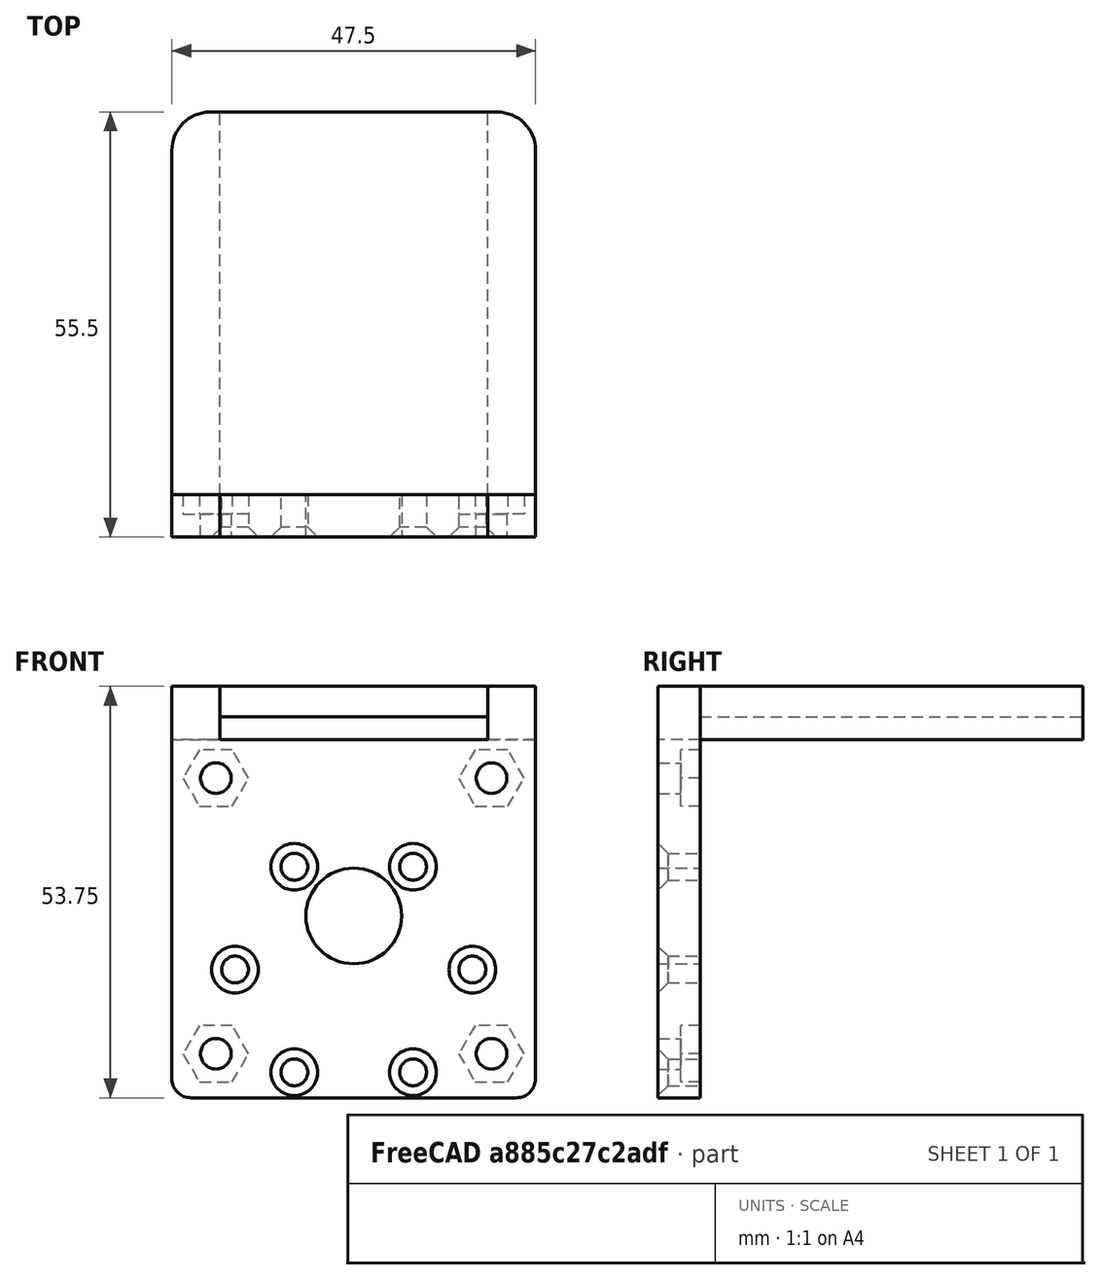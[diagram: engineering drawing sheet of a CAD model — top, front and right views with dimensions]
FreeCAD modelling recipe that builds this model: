
FCSTD DOCUMENT  (FreeCAD 1.0R39109 (Git))
Label: PUMP
License: All rights reserved
LicenseURL: http://en.wikipedia.org/wiki/All_rights_reserved
objects: Sketcher::SketchObject×4, PartDesign::Pad×2, PartDesign::Pocket×2, PartDesign::Body×2, PartDesign::Chamfer×1, Mesh::Feature×1
note: 25 computed .brp shape members not serialized (recipe doc carries the construction recipe); baked Part::Feature solids carry a one-line shape summary decoded from their .brp

FEATURE [Sketcher::SketchObject] Sketch
  ArcFitTolerance = 0
  AttachmentSupport = -> [XZ_Plane001]
  FullyConstrained = false
  MakeInternals = false
  MapMode = 5
  Placement = pos=(0,0,0) rot=(1,0,0;1.5708rad)
  sketch-geometry (46):
    g0: GeomPoint [constr] X=0 Y=0 Z=0
    g1: Circle [constr] CenterX=0 CenterY=0 CenterZ=0 NormalX=0 NormalY=0 NormalZ=1 AngleXU=0 Radius=15.5
    g2: LineSegment [constr] StartX=0 StartY=0 StartZ=0 EndX=-7.75 EndY=13.4234 EndZ=0
    g3: LineSegment [constr] StartX=0 StartY=0 StartZ=0 EndX=0 EndY=15.5 EndZ=0
    g4: Circle CenterX=0 CenterY=7 CenterZ=0 NormalX=0 NormalY=0 NormalZ=1 AngleXU=0 Radius=6.25
    g5: Circle CenterX=-7.75 CenterY=13.4234 CenterZ=0 NormalX=0 NormalY=0 NormalZ=1 AngleXU=0 Radius=1.75
    g6: LineSegment [constr] StartX=-7.75 StartY=13.4234 StartZ=0 EndX=-15.5 EndY=3.6e-15 EndZ=0
    g7: LineSegment [constr] StartX=-15.5 StartY=3.6e-15 StartZ=0 EndX=-7.75 EndY=-13.4234 EndZ=0
    g8: LineSegment [constr] StartX=-7.75 StartY=-13.4234 StartZ=0 EndX=7.75 EndY=-13.4234 EndZ=0
    g9: LineSegment [constr] StartX=7.75 StartY=-13.4234 StartZ=0 EndX=15.5 EndY=-3.6e-15 EndZ=0
    g10: LineSegment [constr] StartX=15.5 StartY=-3.6e-15 StartZ=0 EndX=7.75 EndY=13.4234 EndZ=0
    g11: LineSegment [constr] StartX=7.75 StartY=13.4234 StartZ=0 EndX=-7.75 EndY=13.4234 EndZ=0
    g12: Circle [constr] CenterX=0 CenterY=0 CenterZ=0 NormalX=0 NormalY=0 NormalZ=1 AngleXU=0 Radius=15.5
    g13: Circle CenterX=-15.5 CenterY=3.6e-15 CenterZ=0 NormalX=0 NormalY=0 NormalZ=1 AngleXU=0 Radius=1.75
    g14: Circle CenterX=-7.75 CenterY=-13.4234 CenterZ=0 NormalX=0 NormalY=0 NormalZ=1 AngleXU=0 Radius=1.75
    g15: Circle CenterX=7.75 CenterY=-13.4234 CenterZ=0 NormalX=0 NormalY=0 NormalZ=1 AngleXU=0 Radius=1.75
    g16: Circle CenterX=15.5 CenterY=-3.6e-15 CenterZ=0 NormalX=0 NormalY=0 NormalZ=1 AngleXU=0 Radius=1.75
    g17: Circle CenterX=7.75 CenterY=13.4234 CenterZ=0 NormalX=0 NormalY=0 NormalZ=1 AngleXU=0 Radius=1.75
    g18: LineSegment [constr] StartX=-13.4234 StartY=7.75 StartZ=0 EndX=0 EndY=-15.5 EndZ=0
    g19: LineSegment [constr] StartX=0 StartY=-15.5 StartZ=0 EndX=13.4234 EndY=7.75 EndZ=0
    g20: LineSegment [constr] StartX=13.4234 StartY=7.75 StartZ=0 EndX=-13.4234 EndY=7.75 EndZ=0
    g21: Circle [constr] CenterX=0 CenterY=0 CenterZ=0 NormalX=0 NormalY=0 NormalZ=1 AngleXU=0 Radius=15.5
    g22: Circle [constr] CenterX=0 CenterY=0 CenterZ=0 NormalX=0 NormalY=0 NormalZ=1 AngleXU=0 Radius=18.5
    g23: GeomPoint [constr] X=0 Y=0 Z=0
    g24: LineSegment [constr] StartX=-18 StartY=-11 StartZ=0 EndX=-18 EndY=25 EndZ=0
    g25: LineSegment [constr] StartX=-18 StartY=25 StartZ=0 EndX=18 EndY=25 EndZ=0
    g26: LineSegment [constr] StartX=18 StartY=25 StartZ=0 EndX=18 EndY=-11 EndZ=0
    g27: LineSegment [constr] StartX=18 StartY=-11 StartZ=0 EndX=-18 EndY=-11 EndZ=0
    g28: GeomPoint [constr] X=0 Y=7 Z=0
    g29: Circle CenterX=-18 CenterY=25 CenterZ=0 NormalX=0 NormalY=0 NormalZ=1 AngleXU=0 Radius=2
    g30: Circle CenterX=18 CenterY=25 CenterZ=0 NormalX=0 NormalY=0 NormalZ=1 AngleXU=0 Radius=2
    g31: Circle CenterX=18 CenterY=-11 CenterZ=0 NormalX=0 NormalY=0 NormalZ=1 AngleXU=0 Radius=2
    g32: Circle CenterX=-18 CenterY=-11 CenterZ=0 NormalX=0 NormalY=0 NormalZ=1 AngleXU=0 Radius=2
    g33: LineSegment StartX=21.25 StartY=-16.75 StartZ=0 EndX=-21.25 EndY=-16.75 EndZ=0
    g34: GeomPoint [constr] X=0 Y=7 Z=0
    g35: ArcOfCircle CenterX=-21.25 CenterY=-14.25 CenterZ=0 NormalX=0 NormalY=0 NormalZ=1 AngleXU=0 Radius=2.5 StartAngle=3.14159 EndAngle=4.71239
    g36: GeomPoint [constr] X=-23.75 Y=-16.75 Z=0
    g37: ArcOfCircle CenterX=21.25 CenterY=-14.25 CenterZ=0 NormalX=0 NormalY=0 NormalZ=1 AngleXU=0 Radius=2.5 StartAngle=4.71239 EndAngle=6.28319
    g38: GeomPoint [constr] X=23.75 Y=-16.75 Z=0
    g39: LineSegment StartX=-23.75 StartY=37 StartZ=0 EndX=-17.5 EndY=37 EndZ=0
    g40: LineSegment StartX=-17.5 StartY=37 StartZ=0 EndX=-17.5 EndY=30 EndZ=0
    g41: LineSegment StartX=-17.5 StartY=30 StartZ=0 EndX=17.5 EndY=30 EndZ=0
    g42: LineSegment StartX=17.5 StartY=30 StartZ=0 EndX=17.5 EndY=37 EndZ=0
    g43: LineSegment StartX=17.5 StartY=37 StartZ=0 EndX=23.75 EndY=37 EndZ=0
    g44: LineSegment StartX=23.75 StartY=37 StartZ=0 EndX=23.75 EndY=-14.25 EndZ=0
    g45: LineSegment StartX=-23.75 StartY=37 StartZ=0 EndX=-23.75 EndY=-14.25 EndZ=0
  constraints (103):
    c: Coincident(g0,g-1)
    c: Coincident(g1,g0)
    c: Coincident(g2,g0)
    c: PointOnObject(g2,g1)
    c: Coincident(g3,g0)
    c: PointOnObject(g3,g1)
    c: Vertical(g3)
    c: Angle(g3,g2) = 0.523599
    c: PointOnObject(g4,g3)
    c: DistanceY(g0,g4) = 7
    c: Coincident(g5,g2)
    c: Diameter(g1) = 31
    c: Coincident(g6,g7)
    c: Coincident(g7,g8)
    c: Coincident(g8,g9)
    c: Coincident(g9,g10)
    c: Coincident(g10,g11)
    c: Coincident(g11,g6)
    c: Equal(g6, g7-g11) x5
    c: PointOnObject(g6,g12)
    c: PointOnObject(g7,g12)
    c: PointOnObject(g8,g12)
    c: PointOnObject(g9,g12)
    c: PointOnObject(g10,g12)
    c: PointOnObject(g11,g12)
    c: Coincident(g12,g0)
    c: Coincident(g11,g2)
    c: Coincident(g13,g6)
    c: Coincident(g14,g7)
    c: Coincident(g15,g8)
    c: Coincident(g16,g9)
    c: Coincident(g17,g10)
    c: Equal(g14,g13)
    c: Equal(g13,g5)
    c: Equal(g5,g17)
    c: Equal(g17,g15)
    c: Equal(g15,g16)
    c: Coincident(g18,g19)
    c: Coincident(g19,g20)
    c: Coincident(g20,g18)
    c: Equal(g18,g19)
    c: Equal(g18,g20)
    c: PointOnObject(g18,g21)
    c: PointOnObject(g19,g21)
    c: PointOnObject(g20,g21)
    c: Coincident(g21,g0)
    c: PointOnObject(g20,g1)
    c: Horizontal(g20)
    c: Coincident(g22,g0)
    c: Diameter(g22) = 37
    c: Diameter(g17) = 3.5
    c: Diameter(g4) = 12.5
    c: Coincident(g23,g0)
    c: Coincident(g24,g25)
    c: Coincident(g25,g26)
    c: Coincident(g26,g27)
    c: Coincident(g27,g24)
    c: Horizontal(g25)
    c: Horizontal(g27)
    c: Vertical(g24)
    c: Vertical(g26)
    c: Symmetric(g25,g24,g28)
    c: Coincident(g28,g4)
    c: DistanceX(g25,g25) = 36
    c: Equal(g25,g24)
    c: Coincident(g29,g24)
    c: Coincident(g30,g25)
    c: Coincident(g31,g26)
    c: Coincident(g32,g24)
    c: Equal(g32,g31)
    c: Equal(g31,g29)
    c: Equal(g29,g30)
    c: Diameter(g29) = 4
    c: Horizontal(g33)
    c: Coincident(g34,g4)
    c: DistanceY(g36,g-1) = 16.75
    c: PointOnObject(g36,g33)
    c: Tangent(g33,g35) = 1.5708
    c: PointOnObject(g38,g33)
    c: Tangent(g33,g37) = 1.5708
    c: Diameter(g35) = 5
    c: Horizontal(g39)
    c: Coincident(g39,g40)
    c: Vertical(g40)
    c: Coincident(g40,g41)
    c: Horizontal(g41)
    c: Coincident(g41,g42)
    c: Vertical(g42)
    c: Coincident(g42,g43)
    c: Horizontal(g43)
    c: Equal(g39,g43)
    c: DistanceX(g39,g42) = 35
    c: DistanceX(g39,g43) = 47.5  'width'
    c: Coincident(g44,g43)
    c: Tangent(g44,g37) = 1.5708
    c: Vertical(g44)
    c: Symmetric(g35,g37,g-2)
    c: Horizontal(g42,g39)
    c: Coincident(g45,g39)
    c: Tangent(g45,g35) = -1.5708
    c: Vertical(g45)
    c: DistanceY(g-1,g40) = 30  'Walloffset'
    c: DistanceY(g40,g39) = 7  'wall'
FEATURE [PartDesign::Pad] Pad
  Direction = (0,-1,2e-16)
  Length = 5.5
  Length2 = 10
  Placement = pos=(0,0,0) rot=(1,0,0;1.5708rad)
  Profile = -> Sketch
  ReferenceAxis = -> Sketch [N_Axis]
  Suppressed = false
  Type = 0
FEATURE [PartDesign::Chamfer] Chamfer
  Angle = 45
  Base = -> Pad [Edge63,Edge51,Edge48,Edge60,Edge54,Edge57]
  BaseFeature = -> Pad
  ChamferType = 0
  FlipDirection = false
  Placement = pos=(0,0,0) rot=(1,0,0;1.5708rad)
  Size = 1.3
  Size2 = 1
  SupportTransform = false
  Suppressed = false
  UseAllEdges = false
FEATURE [Sketcher::SketchObject] Sketch001
  ArcFitTolerance = 0
  AttachmentSupport = -> [XZ_Plane001]
  ExternalGeometry = -> [Chamfer]
  FullyConstrained = true
  MakeInternals = false
  MapMode = 5
  Placement = pos=(0,0,0) rot=(1,0,0;1.5708rad)
  sketch-geometry (28):
    g0: LineSegment StartX=-15.8638 StartY=28.7 StartZ=0 EndX=-20.1362 EndY=28.7 EndZ=0
    g1: LineSegment StartX=-20.1362 StartY=28.7 StartZ=0 EndX=-22.2724 EndY=25 EndZ=0
    g2: LineSegment StartX=-22.2724 StartY=25 StartZ=0 EndX=-20.1362 EndY=21.3 EndZ=0
    g3: LineSegment StartX=-20.1362 StartY=21.3 StartZ=0 EndX=-15.8638 EndY=21.3 EndZ=0
    g4: LineSegment StartX=-15.8638 StartY=21.3 StartZ=0 EndX=-13.7276 EndY=25 EndZ=0
    g5: LineSegment StartX=-13.7276 StartY=25 StartZ=0 EndX=-15.8638 EndY=28.7 EndZ=0
    g6: Circle [constr] CenterX=-18 CenterY=25 CenterZ=0 NormalX=0 NormalY=0 NormalZ=1 AngleXU=0 Radius=4.27239
    g7: LineSegment StartX=20.1362 StartY=28.7 StartZ=0 EndX=15.8638 EndY=28.7 EndZ=0
    g8: LineSegment StartX=15.8638 StartY=28.7 StartZ=0 EndX=13.7276 EndY=25 EndZ=0
    g9: LineSegment StartX=13.7276 StartY=25 StartZ=0 EndX=15.8638 EndY=21.3 EndZ=0
    g10: LineSegment StartX=15.8638 StartY=21.3 StartZ=0 EndX=20.1362 EndY=21.3 EndZ=0
    g11: LineSegment StartX=20.1362 StartY=21.3 StartZ=0 EndX=22.2724 EndY=25 EndZ=0
    g12: LineSegment StartX=22.2724 StartY=25 StartZ=0 EndX=20.1362 EndY=28.7 EndZ=0
    g13: Circle [constr] CenterX=18 CenterY=25 CenterZ=0 NormalX=0 NormalY=0 NormalZ=1 AngleXU=0 Radius=4.27239
    g14: LineSegment StartX=20.1362 StartY=-7.3 StartZ=0 EndX=15.8638 EndY=-7.3 EndZ=0
    g15: LineSegment StartX=15.8638 StartY=-7.3 StartZ=0 EndX=13.7276 EndY=-11 EndZ=0
    g16: LineSegment StartX=13.7276 StartY=-11 StartZ=0 EndX=15.8638 EndY=-14.7 EndZ=0
    g17: LineSegment StartX=15.8638 StartY=-14.7 StartZ=0 EndX=20.1362 EndY=-14.7 EndZ=0
    g18: LineSegment StartX=20.1362 StartY=-14.7 StartZ=0 EndX=22.2724 EndY=-11 EndZ=0
    g19: LineSegment StartX=22.2724 StartY=-11 StartZ=0 EndX=20.1362 EndY=-7.3 EndZ=0
    g20: Circle [constr] CenterX=18 CenterY=-11 CenterZ=0 NormalX=0 NormalY=0 NormalZ=1 AngleXU=0 Radius=4.27239
    g21: LineSegment StartX=-15.8638 StartY=-7.3 StartZ=0 EndX=-20.1362 EndY=-7.3 EndZ=0
    g22: LineSegment StartX=-20.1362 StartY=-7.3 StartZ=0 EndX=-22.2724 EndY=-11 EndZ=0
    g23: LineSegment StartX=-22.2724 StartY=-11 StartZ=0 EndX=-20.1362 EndY=-14.7 EndZ=0
    g24: LineSegment StartX=-20.1362 StartY=-14.7 StartZ=0 EndX=-15.8638 EndY=-14.7 EndZ=0
    g25: LineSegment StartX=-15.8638 StartY=-14.7 StartZ=0 EndX=-13.7276 EndY=-11 EndZ=0
    g26: LineSegment StartX=-13.7276 StartY=-11 StartZ=0 EndX=-15.8638 EndY=-7.3 EndZ=0
    g27: Circle [constr] CenterX=-18 CenterY=-11 CenterZ=0 NormalX=0 NormalY=0 NormalZ=1 AngleXU=0 Radius=4.27239
  constraints (64):
    c: Coincident(g0,g1)
    c: Coincident(g1,g2)
    c: Coincident(g2,g3)
    c: Coincident(g3,g4)
    c: Coincident(g4,g5)
    c: Coincident(g5,g0)
    c: Equal(g0, g1-g5) x5
    c: PointOnObject(g0,g6)
    c: PointOnObject(g1,g6)
    c: PointOnObject(g2,g6)
    c: PointOnObject(g3,g6)
    c: PointOnObject(g4,g6)
    c: PointOnObject(g5,g6)
    c: Coincident(g6,g-4)
    c: Coincident(g7,g8)
    c: Coincident(g8,g9)
    c: Coincident(g9,g10)
    c: Coincident(g10,g11)
    c: Coincident(g11,g12)
    c: Coincident(g12,g7)
    c: Equal(g7, g8-g12) x5
    c: PointOnObject(g7,g13)
    c: PointOnObject(g8,g13)
    c: PointOnObject(g9,g13)
    c: PointOnObject(g10,g13)
    c: PointOnObject(g11,g13)
    c: PointOnObject(g12,g13)
    c: Coincident(g13,g-3)
    c: Coincident(g14,g15)
    c: Coincident(g15,g16)
    c: Coincident(g16,g17)
    c: Coincident(g17,g18)
    c: Coincident(g18,g19)
    c: Coincident(g19,g14)
    c: Equal(g14, g15-g19) x5
    c: PointOnObject(g14,g20)
    c: PointOnObject(g15,g20)
    c: PointOnObject(g16,g20)
    c: PointOnObject(g17,g20)
    c: PointOnObject(g18,g20)
    c: PointOnObject(g19,g20)
    c: Coincident(g20,g-6)
    c: Coincident(g21,g22)
    c: Coincident(g22,g23)
    c: Coincident(g23,g24)
    c: Coincident(g24,g25)
    c: Coincident(g25,g26)
    c: Coincident(g26,g21)
    c: Equal(g21, g22-g26) x5
    c: PointOnObject(g21,g27)
    c: PointOnObject(g22,g27)
    c: PointOnObject(g23,g27)
    c: PointOnObject(g24,g27)
    c: PointOnObject(g25,g27)
    c: PointOnObject(g26,g27)
    c: Coincident(g27,g-5)
    c: Equal(g6,g13)
    c: Equal(g20,g6)
    c: Equal(g6,g27)
    c: Horizontal(g21)
    c: Horizontal(g14)
    c: Horizontal(g7)
    c: Horizontal(g0)
    c: DistanceY(g3,g0) = 7.4
FEATURE [PartDesign::Pocket] Pocket
  BaseFeature = -> Chamfer
  Direction = (0,1,-2e-16)
  Length = 2.5
  Length2 = 5
  Placement = pos=(0,0,0) rot=(1,0,0;1.5708rad)
  Profile = -> Sketch001
  ReferenceAxis = -> Sketch001 [N_Axis]
  Reversed = true
  Suppressed = false
  Type = 0
FEATURE [PartDesign::Body] Body001  label="Body"
  AllowCompound = false
  Group = -> [Sketch,Pad,Chamfer,Sketch001,Pocket]
  Origin = -> Origin001
  Tip = -> Pocket
FEATURE [Mesh::Feature] OBJ_PCB001  label="PCB Dispenser V2.003"
  Placement = pos=(0.1548,17.219,26.5186) rot=(0,1,0;3.14159rad)
FEATURE [Sketcher::SketchObject] Sketch006
  ArcFitTolerance = 1e-06
  AttachmentOffset = pos=(0,0,30) rot=(0,0,1;0rad)
  AttachmentSupport = -> [XY_Plane]
  FullyConstrained = true
  MakeInternals = false
  MapMode = 5
  Placement = pos=(0,0,30) rot=(0,0,1;0rad)
  expr: .AttachmentOffset.Base.z = Sketch.Constraints.Walloffset
  expr: Constraints[18] = Sketch.Constraints.width
  sketch-geometry (9):
    g0: LineSegment StartX=-23.75 StartY=0 StartZ=0 EndX=23.75 EndY=0 EndZ=0
    g1: LineSegment StartX=23.75 StartY=0 StartZ=0 EndX=23.75 EndY=45 EndZ=0
    g2: LineSegment StartX=18.75 StartY=50 StartZ=0 EndX=-18.75 EndY=50 EndZ=0
    g3: LineSegment StartX=-23.75 StartY=45 StartZ=0 EndX=-23.75 EndY=0 EndZ=0
    g4: GeomPoint [constr] X=0 Y=25 Z=0
    g5: ArcOfCircle CenterX=-18.75 CenterY=45 CenterZ=0 NormalX=0 NormalY=0 NormalZ=1 AngleXU=0 Radius=5 StartAngle=1.5708 EndAngle=3.14159
    g6: GeomPoint [constr] X=-23.75 Y=50 Z=0
    g7: ArcOfCircle CenterX=18.75 CenterY=45 CenterZ=0 NormalX=0 NormalY=0 NormalZ=1 AngleXU=0 Radius=5 StartAngle=4e-16 EndAngle=1.5708
    g8: GeomPoint [constr] X=23.75 Y=50 Z=0
  constraints (21):
    c: Coincident(g0,g1)
    c: Coincident(g3,g0)
    c: Horizontal(g0)
    c: Horizontal(g2)
    c: Vertical(g1)
    c: Vertical(g3)
    c: Symmetric(g8,g0,g4)
    c: PointOnObject(g4,g-2)
    c: PointOnObject(g6,g2)
    c: PointOnObject(g6,g3)
    c: Tangent(g2,g5) = -1.5708
    c: Tangent(g3,g5) = -1.5708
    c: PointOnObject(g8,g2)
    c: PointOnObject(g8,g1)
    c: Tangent(g2,g7) = -1.5708
    c: Tangent(g1,g7) = -1.5708
    c: Equal(g5,g7)
    c: Diameter(g5) = 10
    c: DistanceX(g0,g0) = 47.5
    c: PointOnObject(g-1,g0)
    c: DistanceY(g-1,g2) = 50
FEATURE [PartDesign::Pad] Pad001
  Direction = (0,0,1)
  Length = 7
  Length2 = 10
  Profile = -> Sketch006
  ReferenceAxis = -> Sketch006 [N_Axis]
  Refine = true
  Suppressed = false
  Type = 0
  expr: Length = Sketch.Constraints.wall
FEATURE [Sketcher::SketchObject] Sketch007
  ArcFitTolerance = 1e-06
  AttachmentSupport = -> [XZ_Plane]
  FullyConstrained = true
  MakeInternals = false
  MapMode = 5
  Placement = pos=(0,0,0) rot=(1,0,0;1.5708rad)
  expr: Constraints[12] = Sketch.Constraints.Walloffset
  sketch-geometry (5):
    g0: LineSegment StartX=-17.5 StartY=33 StartZ=0 EndX=-17.5 EndY=30 EndZ=0
    g1: LineSegment StartX=-17.5 StartY=30 StartZ=0 EndX=17.5 EndY=30 EndZ=0
    g2: LineSegment StartX=17.5 StartY=30 StartZ=0 EndX=17.5 EndY=33 EndZ=0
    g3: LineSegment StartX=17.5 StartY=33 StartZ=0 EndX=-17.5 EndY=33 EndZ=0
    g4: GeomPoint [constr] X=0 Y=31.5 Z=0
  constraints (13):
    c: Coincident(g0,g1)
    c: Coincident(g1,g2)
    c: Coincident(g2,g3)
    c: Coincident(g3,g0)
    c: Vertical(g0)
    c: Vertical(g2)
    c: Horizontal(g1)
    c: Horizontal(g3)
    c: Symmetric(g2,g0,g4)
    c: PointOnObject(g4,g-2)
    c: DistanceX(g3,g3) = 35
    c: DistanceY(g2,g2) = 3
    c: DistanceY(g-1,g1) = 30
FEATURE [PartDesign::Pocket] Pocket001
  BaseFeature = -> Pad001
  Direction = (0,1,-2e-16)
  Length = 5
  Length2 = 5
  Midplane = true
  Profile = -> Sketch007
  ReferenceAxis = -> Sketch007 [N_Axis]
  Refine = true
  Suppressed = false
  Type = 1
FEATURE [PartDesign::Body] Body  label="Body001"
  AllowCompound = false
  Group = -> [Sketch006,Pad001,Sketch007,Pocket001]
  Origin = -> Origin
  Tip = -> Pocket001
